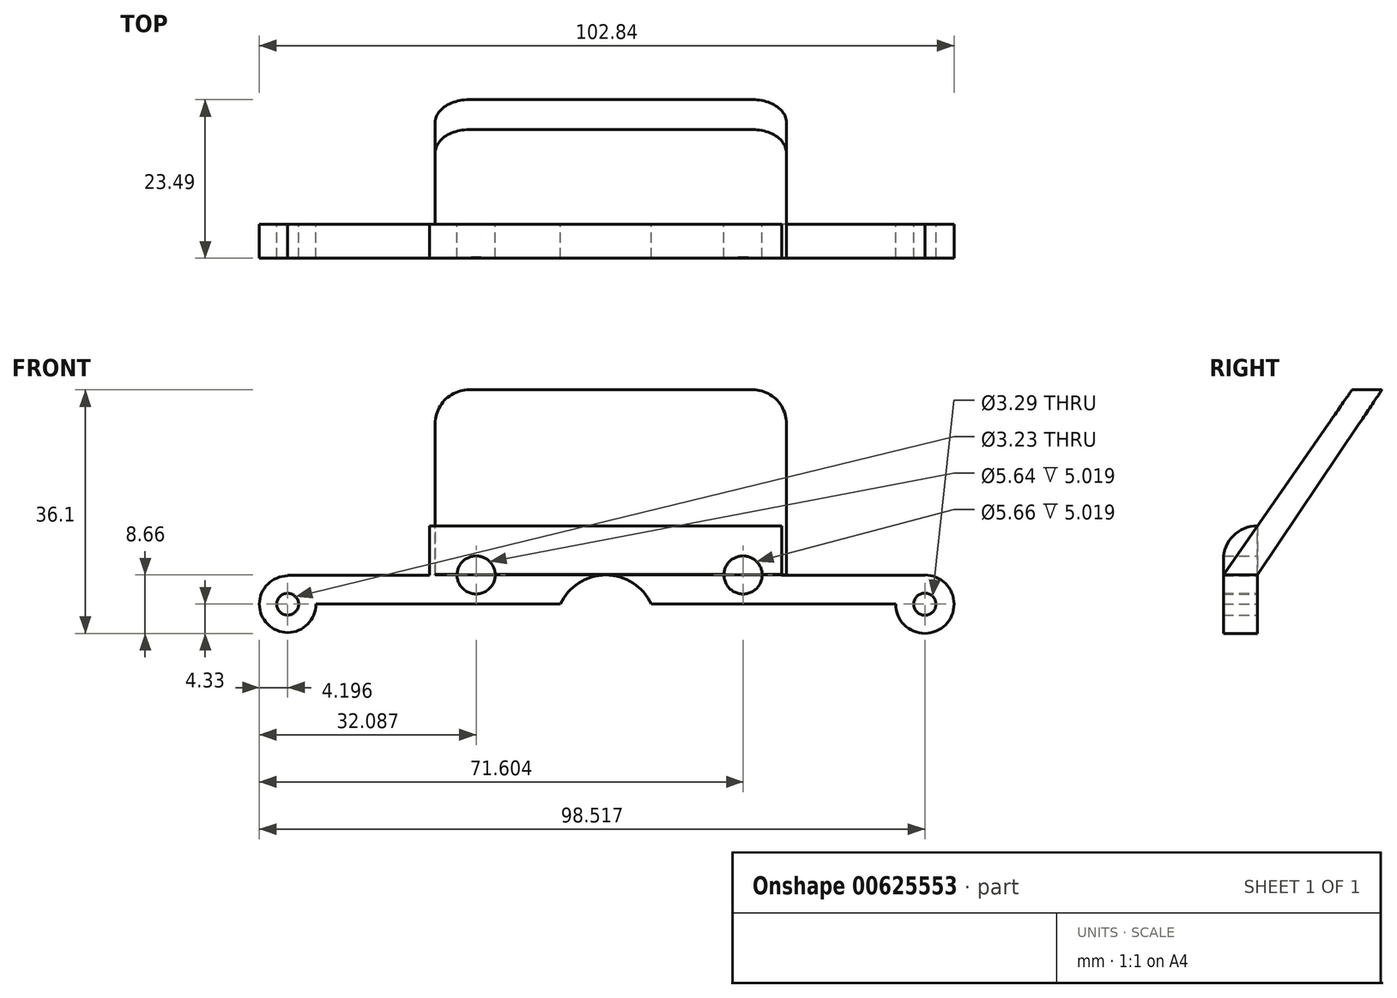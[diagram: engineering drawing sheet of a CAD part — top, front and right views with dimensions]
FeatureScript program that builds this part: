
annotation { "Feature Type Name" : "Feature", "Feature Type Description" : "" }
export const myFeature = defineFeature(function(context is Context, id is Id, definition is map)
    precondition{}
    {
        {
            var Q0;
            Q0=qCreatedBy(makeId("Front.planeOp"),FACE);
            var sketch = newSketch(context, id + "F0", { "sketchPlane" : qUnion([Q0])});
            skLineSegment(sketch, "E0.bottom", {"start": v(45.16, -8.68) * mm, "end": v(-40.64, -8.68) * mm});
            skLineSegment(sketch, "E0.top", {"start": v(28.3, 21.2) * mm, "end": v(-23.85, 21.2) * mm});
            skLineSegment(sketch, "E0.right", {"start": v(-44.83, -4.49) * mm, "end": v(-44.83, -4.4) * mm});
            skArc(sketch, "E1", {"start": v(45.16, -8.68) * mm, "mid": v(52.55, -11.74) * mm, "end": v(49.49, -4.36) * mm});
            skArc(sketch, "E2", {"start": v(-44.83, -4.49) * mm, "mid": v(-47.8, -11.65) * mm, "end": v(-40.64, -8.68) * mm});
            skCircle(sketch, "E3", {"center": v(49.49, -8.68) * mm, "radius": 1.65 * mm});
            skCircle(sketch, "E4", {"center": v(-44.83, -8.68) * mm, "radius": 1.61 * mm});
            skLineSegment(sketch, "E5.top", {"start": v(49.49, -4.4) * mm, "end": v(28.3, -4.4) * mm});
            skLineSegment(sketch, "E5.left", {"start": v(49.49, -4.36) * mm, "end": v(49.49, -4.4) * mm});
            skLineSegment(sketch, "E5.right", {"start": v(28.3, 21.2) * mm, "end": v(28.3, -4.4) * mm});
            skLineSegment(sketch, "E6.top", {"start": v(-44.83, -4.4) * mm, "end": v(-23.85, -4.4) * mm});
            skLineSegment(sketch, "E6.right", {"start": v(-23.85, 21.2) * mm, "end": v(-23.85, -4.4) * mm});
            skSolve(sketch);
        }
        {
            var Q0;
            Q0 = qSketchRegion(id + "F0", true);
            extrude(context, id + "F1", {"entities" : qUnion([Q0]), "depth" : 5 * mm, "offsetDistance" : 25 * mm});
        }
        {
            var Q0;
            Q0=qCreatedBy(makeId("Right.planeOp"),FACE);
            cPlane(context, id + "F2", {"entities" : qUnion([Q0]), "cplaneType" : CPlaneType.OFFSET, "offset" : 29 * mm, "width" : 150 * mm, "height" : 150 * mm});
        }
        {
            var Q0;
            Q0=qCreatedBy(id+"F2.planeOp",FACE);
            var sketch = newSketch(context, id + "F3", { "sketchPlane" : qUnion([Q0])});
            skLineSegment(sketch, "E7", {"start": v(-5.02, -4.32) * mm, "end": v(14.04, 23.1) * mm});
            skLineSegment(sketch, "E8", {"start": v(14.04, 23.1) * mm, "end": v(18.47, 23.1) * mm});
            skLineSegment(sketch, "E9", {"start": v(18.47, 23.1) * mm, "end": v(0, -4.35) * mm});
            skLineSegment(sketch, "E10", {"start": v(0, -4.35) * mm, "end": v(-5.02, -4.32) * mm});
            skSolve(sketch);
        }
        {
            var Q0;
            Q0 = qSketchRegion(id + "F3", true);
            extrude(context, id + "F4", {"entities" : qUnion([Q0]), "operationType" : NewBodyOperationType.ADD, "oppositeDirection" : true, "depth" : 52 * mm, "offsetDistance" : 25 * mm});
        }
        {
            var Q0;
            Q0=qCreatedBy(id+"F2.planeOp",FACE);
            var sketch = newSketch(context, id + "F5", { "sketchPlane" : qUnion([Q0])});
            skLineSegment(sketch, "E11.bottom", {"start": v(-5.12, 21.4) * mm, "end": v(0, 21.4) * mm});
            skLineSegment(sketch, "E11.top", {"start": v(-5.12, 2.92) * mm, "end": v(0, 2.92) * mm});
            skLineSegment(sketch, "E11.left", {"start": v(-5.12, 21.4) * mm, "end": v(-5.12, 2.92) * mm});
            skLineSegment(sketch, "E11.right", {"start": v(0, 21.4) * mm, "end": v(0, 2.92) * mm});
            skSolve(sketch);
        }
        {
            var Q0;
            Q0 = qSketchRegion(id + "F5", true);
            extrude(context, id + "F6", {"entities" : qUnion([Q0]), "operationType" : NewBodyOperationType.REMOVE, "endBound" : BoundingType.THROUGH_ALL, "oppositeDirection" : true, "depth" : 25 * mm, "offsetDistance" : 25 * mm});
        }
        {
            var Q0;
            Q0=makeQuery(id+"F4.opExtrude","CAP_EDGE",EDGE,{"disambiguationData":[OSD([sQuery(id+"F3.wireOp",EDGE,"E8")])],"isStart":false});
            var Q1;
            Q1=makeQuery(id+"F4.opExtrude","CAP_EDGE",EDGE,{"disambiguationData":[OSD([sQuery(id+"F3.wireOp",EDGE,"E8")])],"isStart":true});
            var Q2;
            Q2=makeQuery(id+"F6.boolean.opBoolean","INTERSECT",EDGE,{"derivedFrom":[makeQuery(id+"F1.opExtrude","CAP_FACE",FACE,{"disambiguationData":[OSD([sQuery(id+"F0.wireOp",EDGE,"E0.bottom"),sQuery(id+"F0.wireOp",EDGE,"E0.top"),sQuery(id+"F0.wireOp",EDGE,"E0.right"),sQuery(id+"F0.wireOp",EDGE,"E1"),sQuery(id+"F0.wireOp",EDGE,"E2"),sQuery(id+"F0.wireOp",EDGE,"E3"),sQuery(id+"F0.wireOp",EDGE,"E4"),sQuery(id+"F0.wireOp",EDGE,"E5.top"),sQuery(id+"F0.wireOp",EDGE,"E5.left"),sQuery(id+"F0.wireOp",EDGE,"E5.right"),sQuery(id+"F0.wireOp",EDGE,"E6.top"),sQuery(id+"F0.wireOp",EDGE,"E6.right")])],"isStart":false}),makeQuery(id+"F6.opExtrude","SWEPT_FACE",FACE,{"disambiguationData":[OSD([sQuery(id+"F5.wireOp",EDGE,"E11.top")])]})]});
            fillet(context, id + "F7", {"entities" : qUnion([Q0, Q1, Q2]), "radius" : 5 * mm, "tangentPropagation" : true, "allowEdgeOverflow" : false});
        }
        {
            var Q0;
            Q0=makeQuery(id+"F1.opExtrude","CAP_FACE",FACE,{"disambiguationData":[OSD([sQuery(id+"F0.wireOp",EDGE,"E0.bottom"),sQuery(id+"F0.wireOp",EDGE,"E0.top"),sQuery(id+"F0.wireOp",EDGE,"E0.right"),sQuery(id+"F0.wireOp",EDGE,"E1"),sQuery(id+"F0.wireOp",EDGE,"E2"),sQuery(id+"F0.wireOp",EDGE,"E3"),sQuery(id+"F0.wireOp",EDGE,"E4"),sQuery(id+"F0.wireOp",EDGE,"E5.top"),sQuery(id+"F0.wireOp",EDGE,"E5.left"),sQuery(id+"F0.wireOp",EDGE,"E5.right"),sQuery(id+"F0.wireOp",EDGE,"E6.top"),sQuery(id+"F0.wireOp",EDGE,"E6.right")])],"isStart":true});
            var sketch = newSketch(context, id + "F8", { "sketchPlane" : qUnion([Q0])});
            skCircle(sketch, "E12", {"center": v(-22.57, -4.35) * mm, "radius": 2.83 * mm});
            skCircle(sketch, "E13", {"center": v(16.94, -4.35) * mm, "radius": 2.82 * mm});
            skCircle(sketch, "E14", {"center": v(-2.26, -11.75) * mm, "radius": 7.39 * mm});
            skPoint(sketch, "E14.centerSnap0", {"position": v(-2.26, -8.68) * mm});
            skSolve(sketch);
        }
        {
            var Q0;
            Q0 = qSketchRegion(id + "F8", true);
            extrude(context, id + "F9", {"entities" : qUnion([Q0]), "operationType" : NewBodyOperationType.REMOVE, "oppositeDirection" : true, "depth" : 25 * mm, "offsetDistance" : 25 * mm});
        }
    });
